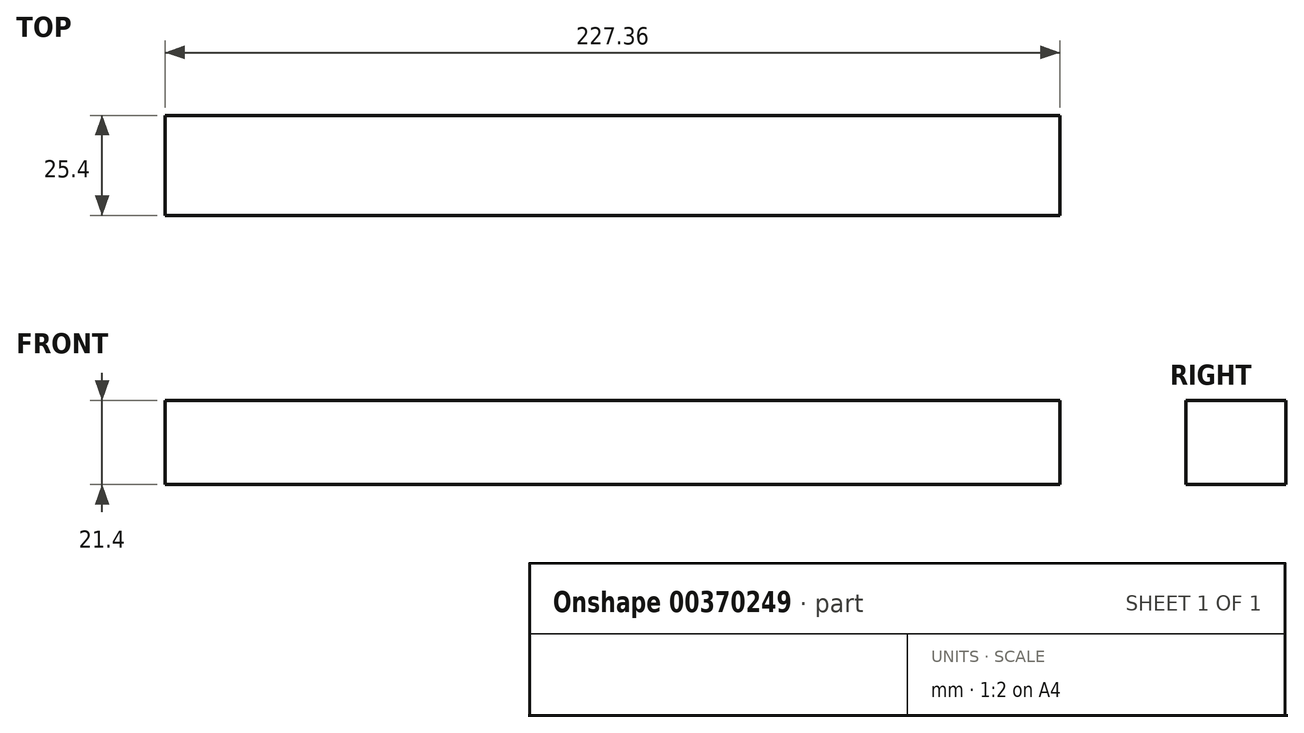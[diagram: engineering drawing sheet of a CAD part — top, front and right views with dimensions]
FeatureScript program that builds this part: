
annotation { "Feature Type Name" : "Feature", "Feature Type Description" : "" }
export const myFeature = defineFeature(function(context is Context, id is Id, definition is map)
    precondition{}
    {
        {
            var Q0;
            Q0=qCreatedBy(makeId("Front.planeOp"),FACE);
            var sketch = newSketch(context, id + "F0", { "sketchPlane" : qUnion([Q0])});
            skLineSegment(sketch, "E0.bottom", {"start": v(-113.68, 10.7) * mm, "end": v(113.68, 10.7) * mm});
            skLineSegment(sketch, "E0.top", {"start": v(-113.68, -10.7) * mm, "end": v(113.68, -10.7) * mm});
            skLineSegment(sketch, "E0.left", {"start": v(-113.68, 10.7) * mm, "end": v(-113.68, -10.7) * mm});
            skLineSegment(sketch, "E0.right", {"start": v(113.68, 10.7) * mm, "end": v(113.68, -10.7) * mm});
            skPoint(sketch, "E0.middle", {"position": v(0, 0) * mm});
            skSolve(sketch);
        }
        {
            var Q0;
            Q0=makeQuery(id+"F0.imprint","IMPRINT",FACE,{"disambiguationData":[TD([[makeQuery(id+"F0.imprint","IMPRINT",EDGE,{"derivedFrom":sQuery(id+"F0.wireOp",EDGE,"E0.bottom")}),-1.0]])]});
            extrude(context, id + "F1", {"entities" : qUnion([Q0]), "oppositeDirection" : true, "depth" : 25.4 * mm});
        }
    });
